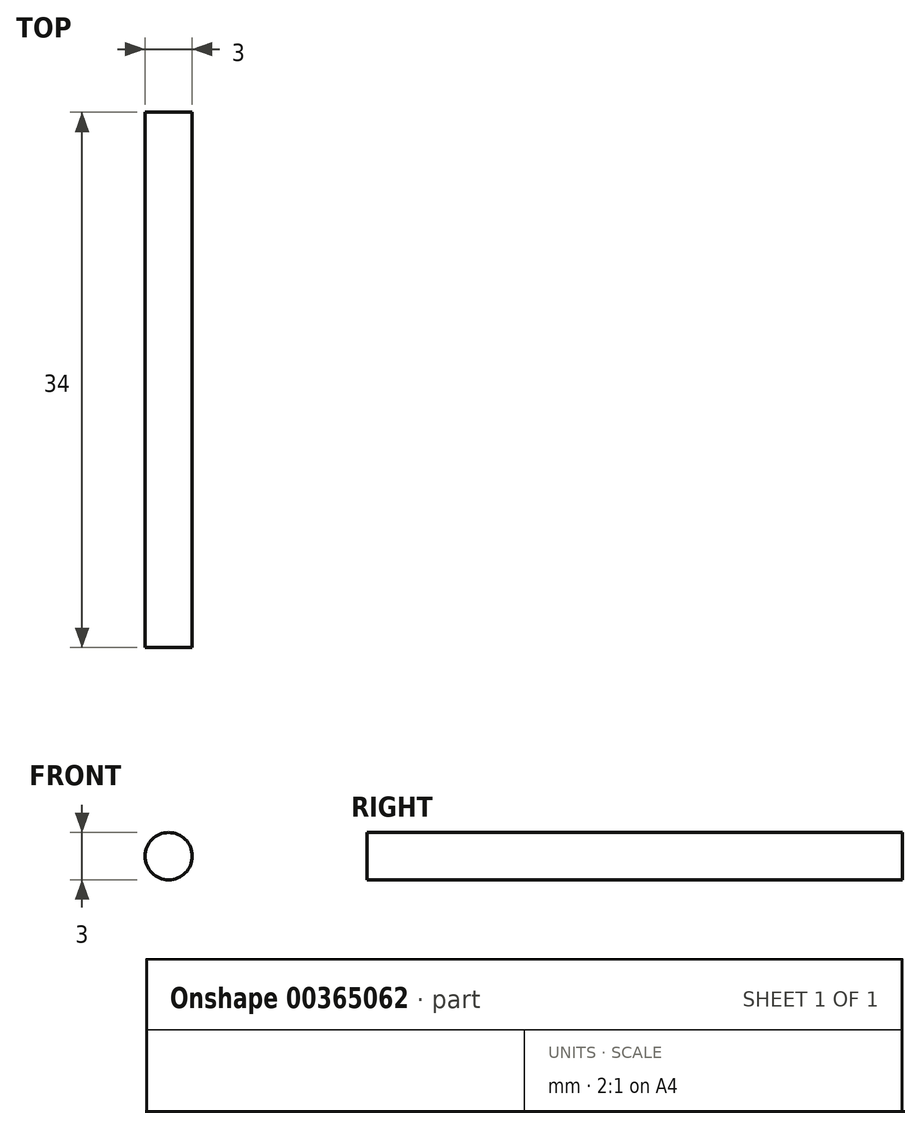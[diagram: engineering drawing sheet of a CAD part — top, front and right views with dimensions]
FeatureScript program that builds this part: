
annotation { "Feature Type Name" : "Feature", "Feature Type Description" : "" }
export const myFeature = defineFeature(function(context is Context, id is Id, definition is map)
    precondition{}
    {
        {
            var Q0;
            Q0=qCreatedBy(makeId("Front.planeOp"),FACE);
            var sketch = newSketch(context, id + "F0", { "sketchPlane" : qUnion([Q0])});
            skCircle(sketch, "E0", {"center": v(0, -0.22) * mm, "radius": 1.5 * mm});
            skSolve(sketch);
        }
        {
            var Q0;
            Q0=makeQuery(id+"F0.imprint","IMPRINT",FACE,{"disambiguationData":[TD([[makeQuery(id+"F0.imprint","IMPRINT",EDGE,{"derivedFrom":sQuery(id+"F0.wireOp",EDGE,"E0")}),1.0]])]});
            extrude(context, id + "F1", {"entities" : qUnion([Q0]), "endBound" : BoundingType.SYMMETRIC, "depth" : 34 * mm});
        }
    });
